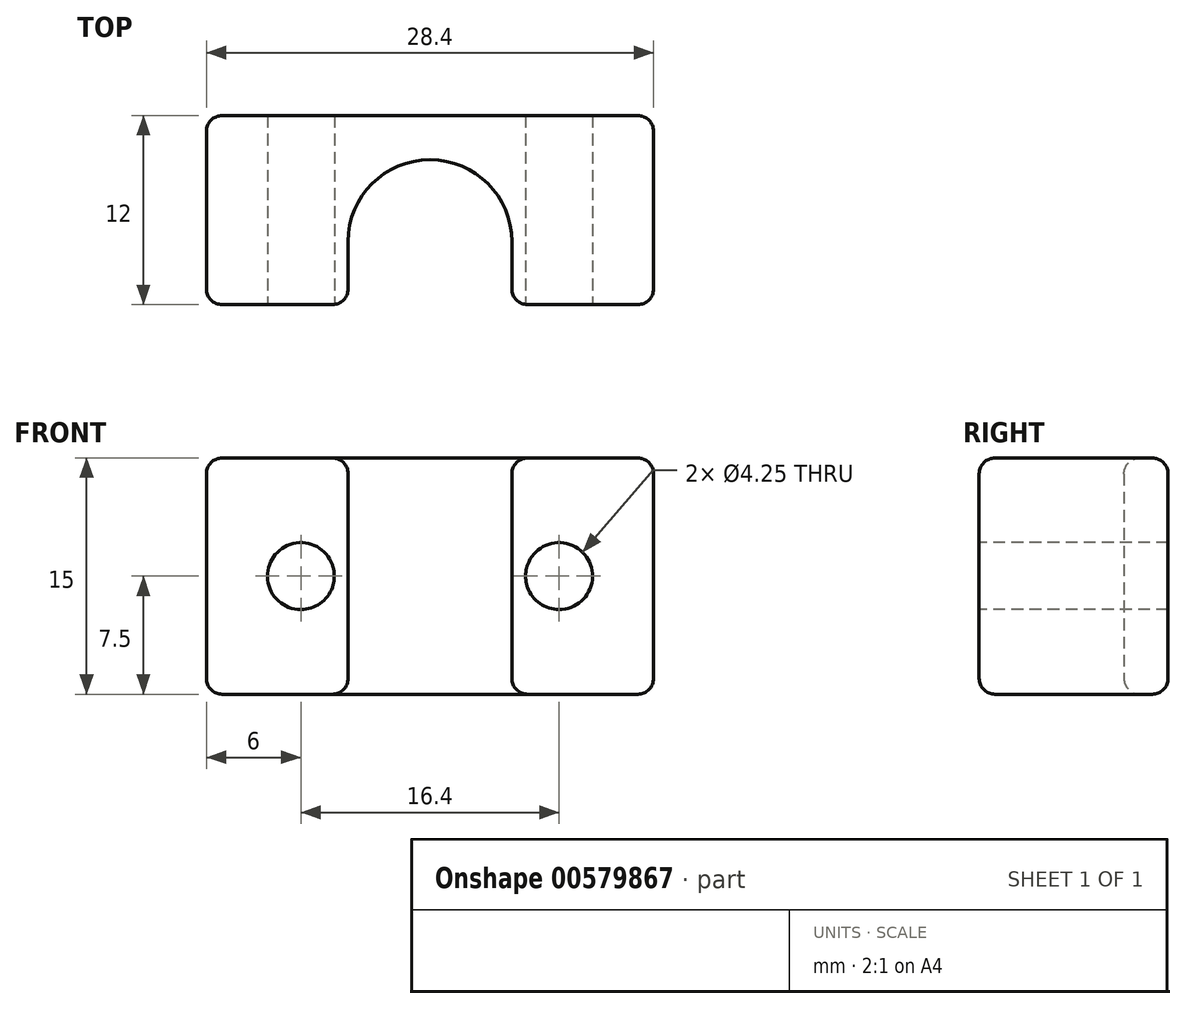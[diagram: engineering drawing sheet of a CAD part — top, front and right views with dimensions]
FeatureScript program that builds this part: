
annotation { "Feature Type Name" : "Feature", "Feature Type Description" : "" }
export const myFeature = defineFeature(function(context is Context, id is Id, definition is map)
    precondition{}
    {
        {
            var Q0;
            Q0=qCreatedBy(makeId("Top.planeOp"),FACE);
            var sketch = newSketch(context, id + "F0", { "sketchPlane" : qUnion([Q0])});
            skLineSegment(sketch, "E0", {"start": v(5.2, 0) * mm, "end": v(14.2, 0) * mm});
            skLineSegment(sketch, "E1", {"start": v(14.2, 0) * mm, "end": v(14.2, 12) * mm});
            skLineSegment(sketch, "E2", {"start": v(14.2, 12) * mm, "end": v(-14.2, 12) * mm});
            skLineSegment(sketch, "E3", {"start": v(-14.2, 12) * mm, "end": v(-14.2, 0) * mm});
            skLineSegment(sketch, "E4", {"start": v(-14.2, 0) * mm, "end": v(-5.2, 0) * mm});
            skLineSegment(sketch, "E5", {"start": v(-5.2, 0) * mm, "end": v(-5.2, 4) * mm});
            skArc(sketch, "E6", {"start": v(-5.2, 4) * mm, "mid": v(0, 9.2) * mm, "end": v(5.2, 4) * mm});
            skLineSegment(sketch, "E7", {"start": v(5.2, 4) * mm, "end": v(5.2, 0) * mm});
            skSolve(sketch);
        }
        {
            var Q0;
            Q0 = qSketchRegion(id + "F0", true);
            extrude(context, id + "F1", {"entities" : qUnion([Q0]), "depth" : 15 * mm, "offsetDistance" : 25 * mm});
        }
        {
            var Q0;
            Q0=makeQuery(id+"F1.opExtrude","SWEPT_FACE",FACE,{"disambiguationData":[OSD([sQuery(id+"F0.wireOp",EDGE,"E4")])]});
            var sketch = newSketch(context, id + "F2", { "sketchPlane" : qUnion([Q0])});
            skCircle(sketch, "E8", {"center": v(-8.2, 7.5) * mm, "radius": 2.12 * mm});
            skLineSegment(sketch, "E9", {"start": v(-8.2, 7.5) * mm, "end": v(-8.2, 15) * mm, "construction": true});
            skLineSegment(sketch, "E10", {"start": v(-8.2, 7.5) * mm, "end": v(-8.2, 0) * mm, "construction": true});
            skCircle(sketch, "E11.MirrorC", {"center": v(8.2, 7.5) * mm, "radius": 2.12 * mm});
            skSolve(sketch);
        }
        {
            var Q0;
            Q0 = qSketchRegion(id + "F2", true);
            extrude(context, id + "F3", {"entities" : qUnion([Q0]), "operationType" : NewBodyOperationType.REMOVE, "endBound" : BoundingType.THROUGH_ALL, "oppositeDirection" : true, "depth" : 25 * mm, "offsetDistance" : 25 * mm});
        }
        {
            var Q0;
            Q0=makeQuery(id+"F1.opExtrude","CAP_FACE",FACE,{"disambiguationData":[OSD([sQuery(id+"F0.wireOp",EDGE,"E0"),sQuery(id+"F0.wireOp",EDGE,"E1"),sQuery(id+"F0.wireOp",EDGE,"E2"),sQuery(id+"F0.wireOp",EDGE,"E3"),sQuery(id+"F0.wireOp",EDGE,"E4"),sQuery(id+"F0.wireOp",EDGE,"E5"),sQuery(id+"F0.wireOp",EDGE,"E6"),sQuery(id+"F0.wireOp",EDGE,"E7")])],"isStart":false});
            var Q1;
            Q1=makeQuery(id+"F1.opExtrude","SWEPT_FACE",FACE,{"disambiguationData":[OSD([sQuery(id+"F0.wireOp",EDGE,"E3")])]});
            var Q2;
            Q2=makeQuery(id+"F1.opExtrude","CAP_FACE",FACE,{"disambiguationData":[OSD([sQuery(id+"F0.wireOp",EDGE,"E0"),sQuery(id+"F0.wireOp",EDGE,"E1"),sQuery(id+"F0.wireOp",EDGE,"E2"),sQuery(id+"F0.wireOp",EDGE,"E3"),sQuery(id+"F0.wireOp",EDGE,"E4"),sQuery(id+"F0.wireOp",EDGE,"E5"),sQuery(id+"F0.wireOp",EDGE,"E6"),sQuery(id+"F0.wireOp",EDGE,"E7")])],"isStart":true});
            var Q3;
            Q3=makeQuery(id+"F1.opExtrude","SWEPT_FACE",FACE,{"disambiguationData":[OSD([sQuery(id+"F0.wireOp",EDGE,"E1")])]});
            var Q4;
            Q4=makeQuery(id+"F1.opExtrude","SWEPT_EDGE",EDGE,{"disambiguationData":[OSD([sQuery(id+"F0.wireOp",EDGE,"E4"),sQuery(id+"F0.wireOp",EDGE,"E5")])]});
            var Q5;
            Q5=makeQuery(id+"F1.opExtrude","SWEPT_EDGE",EDGE,{"disambiguationData":[OSD([sQuery(id+"F0.wireOp",EDGE,"E0"),sQuery(id+"F0.wireOp",EDGE,"E7")])]});
            fillet(context, id + "F4", {"entities" : qUnion([Q0, Q1, Q2, Q3, Q4, Q5]), "radius" : 1 * mm, "tangentPropagation" : true, "allowEdgeOverflow" : false});
        }
    });
